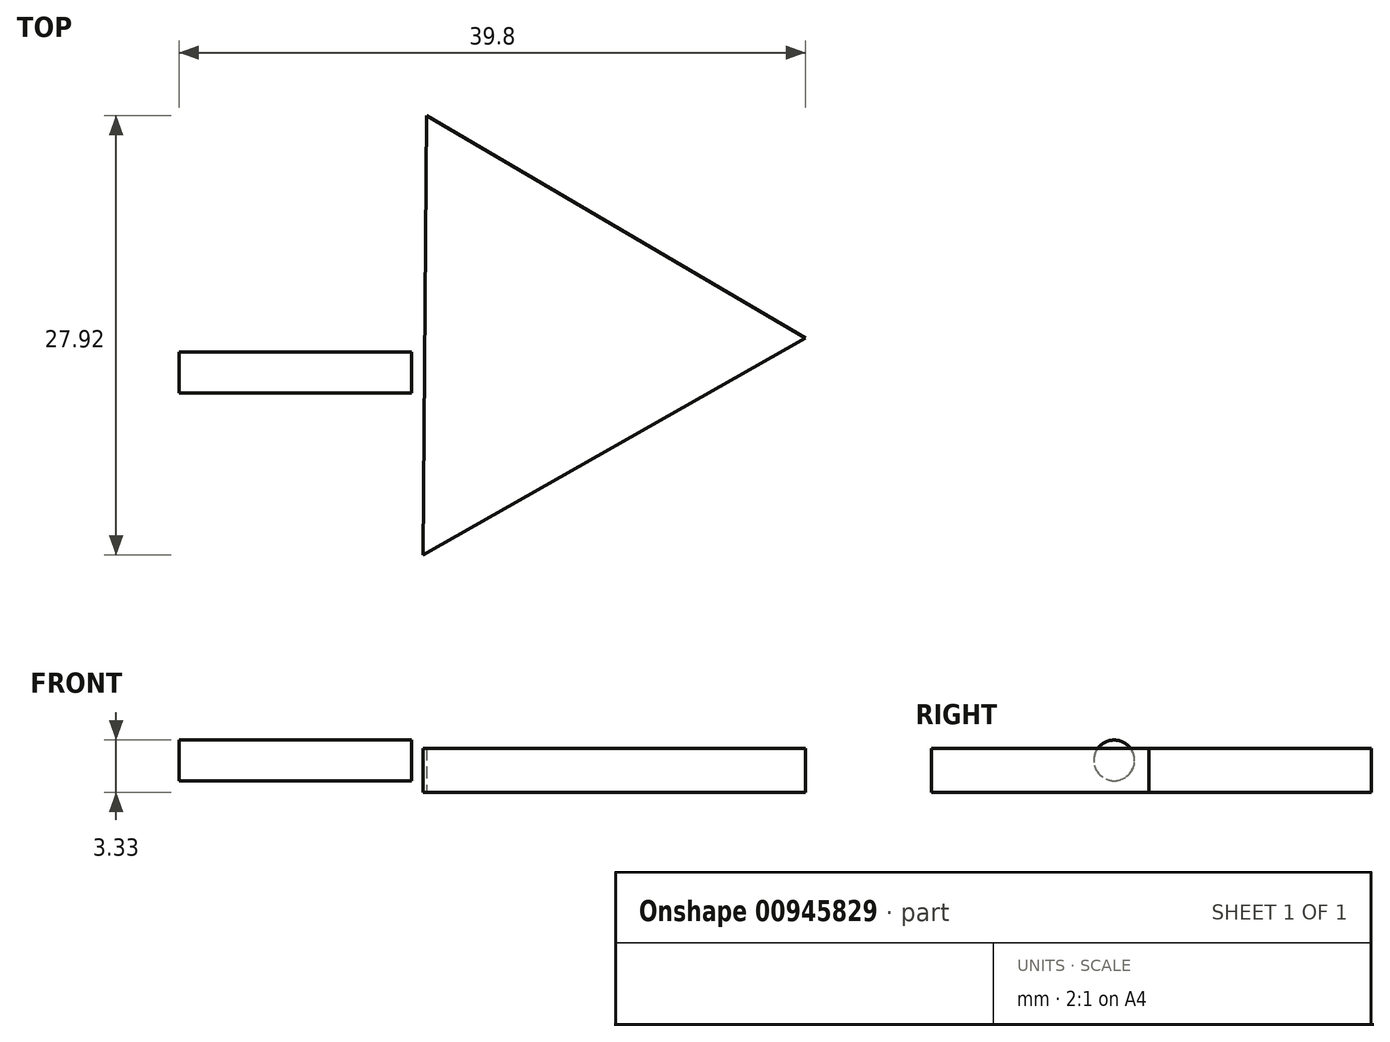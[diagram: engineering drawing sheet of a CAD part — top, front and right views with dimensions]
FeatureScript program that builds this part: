
annotation { "Feature Type Name" : "Feature", "Feature Type Description" : "" }
export const myFeature = defineFeature(function(context is Context, id is Id, definition is map)
    precondition{}
    {
        {
            var Q0;
            Q0=qCreatedBy(makeId("Top.planeOp"),FACE);
            var sketch = newSketch(context, id + "F0", { "sketchPlane" : qUnion([Q0])});
            skCircle(sketch, "E0.cCircle", {"center": v(-121.03, 0) * mm, "radius": 16.12 * mm, "construction": true});
            skLineSegment(sketch, "E0.0", {"start": v(-129.19, -13.9) * mm, "end": v(-128.99, 14.02) * mm});
            skLineSegment(sketch, "E0.1", {"start": v(-128.99, 14.02) * mm, "end": v(-104.9, -0.11) * mm});
            skLineSegment(sketch, "E0.2", {"start": v(-104.9, -0.11) * mm, "end": v(-129.19, -13.9) * mm});
            skSolve(sketch);
        }
        {
            var Q0;
            Q0=makeQuery(id+"F0.imprint","IMPRINT",FACE,{"disambiguationData":[TD([[makeQuery(id+"F0.imprint","IMPRINT",EDGE,{"derivedFrom":sQuery(id+"F0.wireOp",EDGE,"E0.0")}),-1.0]])]});
            extrude(context, id + "F1", {"entities" : qUnion([Q0]), "depth" : 2.8 * mm, "offsetDistance" : 25.4 * mm});
        }
        {
            var Q0;
            Q0=makeQuery(id+"F1.opExtrude","CAP_FACE",FACE,{"disambiguationData":[OSD([sQuery(id+"F0.wireOp",EDGE,"E0.0"),sQuery(id+"F0.wireOp",EDGE,"E0.1"),sQuery(id+"F0.wireOp",EDGE,"E0.2")])],"isStart":false});
            cPlane(context, id + "F2", {"entities" : qUnion([Q0]), "cplaneType" : CPlaneType.OFFSET, "offset" : 0.76 * mm, "oppositeDirection" : true, "width" : 152.4 * mm, "height" : 152.4 * mm});
        }
        {
            var Q0;
            Q0=qCreatedBy(id+"F2.planeOp",FACE);
            var sketch = newSketch(context, id + "F3", { "sketchPlane" : qUnion([Q0])});
            skLineSegment(sketch, "E1.bottom", {"start": v(-129.92, -2.3) * mm, "end": v(-144.7, -2.3) * mm});
            skLineSegment(sketch, "E1.top", {"start": v(-129.92, -3.6) * mm, "end": v(-144.7, -3.6) * mm});
            skLineSegment(sketch, "E1.left", {"start": v(-129.92, -2.3) * mm, "end": v(-129.92, -3.6) * mm});
            skLineSegment(sketch, "E1.right", {"start": v(-144.7, -2.3) * mm, "end": v(-144.7, -3.6) * mm});
            skSolve(sketch);
        }
        {
            var Q0;
            Q0=makeQuery(id+"F3.imprint","IMPRINT",FACE,{"disambiguationData":[TD([[makeQuery(id+"F3.imprint","IMPRINT",EDGE,{"derivedFrom":sQuery(id+"F3.wireOp",EDGE,"E1.bottom")}),1.0]])]});
            var Q1;
            Q1=sQuery(id+"F3.wireOp",EDGE,"E1.bottom");
            revolve(context, id + "F4", {"surfaceOperationType" : NewSurfaceOperationType.NEW, "entities" : qUnion([Q0]), "axis" : qUnion([Q1]), "revolveType" : RevolveType.FULL});
        }
    });
